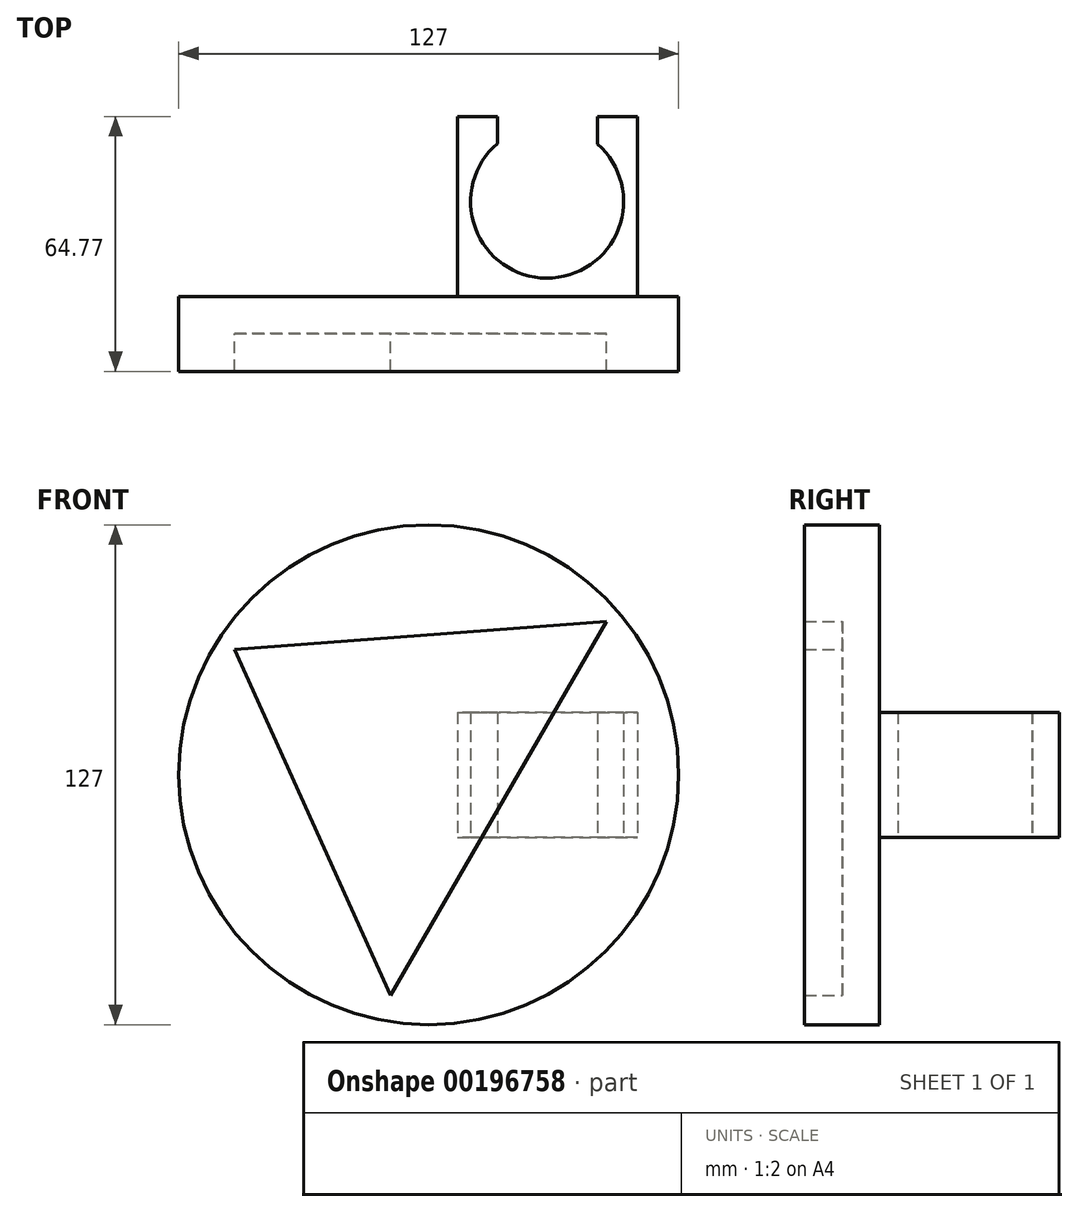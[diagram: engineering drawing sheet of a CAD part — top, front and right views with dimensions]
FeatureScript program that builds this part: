
annotation { "Feature Type Name" : "Feature", "Feature Type Description" : "" }
export const myFeature = defineFeature(function(context is Context, id is Id, definition is map)
    precondition{}
    {
        {
            var Q0;
            Q0=qCreatedBy(makeId("Front.planeOp"),FACE);
            var sketch = newSketch(context, id + "F0", { "sketchPlane" : qUnion([Q0])});
            skCircle(sketch, "E0", {"center": v(0, 0) * mm, "radius": 63.5 * mm});
            skPoint(sketch, "E1.orphan", {"position": v(0, 10.52) * mm});
            skPoint(sketch, "E2.end.orphan", {"position": v(-40.1, 0) * mm});
            skLineSegment(sketch, "E3", {"start": v(45.17, 38.94) * mm, "end": v(-9.64, -56) * mm});
            skLineSegment(sketch, "E4", {"start": v(-9.64, -56) * mm, "end": v(-49.29, 31.86) * mm});
            skLineSegment(sketch, "E5", {"start": v(-49.29, 31.86) * mm, "end": v(45.17, 38.94) * mm});
            skSolve(sketch);
        }
        {
            var Q0;
            Q0 = qSketchRegion(id + "F0", true);
            extrude(context, id + "F1", {"entities" : qUnion([Q0]), "depth" : 19.05 * mm});
        }
        {
            var Q0;
            Q0=makeQuery(id+"F0.imprint","IMPRINT",FACE,{"disambiguationData":[TD([[makeQuery(id+"F0.imprint","IMPRINT",EDGE,{"derivedFrom":sQuery(id+"F0.wireOp",EDGE,"E3")}),-1.0]])]});
            extrude(context, id + "F2", {"entities" : qUnion([Q0]), "operationType" : NewBodyOperationType.ADD, "depth" : 9.4 * mm});
        }
        {
            var Q0;
            Q0=qCreatedBy(makeId("Top.planeOp"),FACE);
            var sketch = newSketch(context, id + "F3", { "sketchPlane" : qUnion([Q0])});
            skLineSegment(sketch, "E6.bottom", {"start": v(53.05, 0) * mm, "end": v(7.33, 0) * mm});
            skLineSegment(sketch, "E7", {"start": v(7.33, 0) * mm, "end": v(7.33, 45.72) * mm});
            skLineSegment(sketch, "E8", {"start": v(7.33, 45.72) * mm, "end": v(17.5, 45.72) * mm});
            skLineSegment(sketch, "E9", {"start": v(53.05, 45.72) * mm, "end": v(53.05, 0) * mm});
            skArc(sketch, "E10", {"start": v(17.5, 38.84) * mm, "mid": v(29.97, 4.62) * mm, "end": v(42.9, 38.68) * mm});
            skLineSegment(sketch, "E11.trimOffspring", {"start": v(42.9, 45.72) * mm, "end": v(53.05, 45.72) * mm});
            skLineSegment(sketch, "E12.trimOffspring", {"start": v(17.5, 38.84) * mm, "end": v(17.5, 45.72) * mm});
            skLineSegment(sketch, "E13.trimOffspring", {"start": v(42.9, 38.68) * mm, "end": v(42.9, 45.72) * mm});
            skSolve(sketch);
        }
        {
            var Q0;
            Q0 = qSketchRegion(id + "F3", true);
            extrude(context, id + "F4", {"entities" : qUnion([Q0]), "operationType" : NewBodyOperationType.ADD, "endBound" : BoundingType.SYMMETRIC, "depth" : 31.75 * mm});
        }
    });
